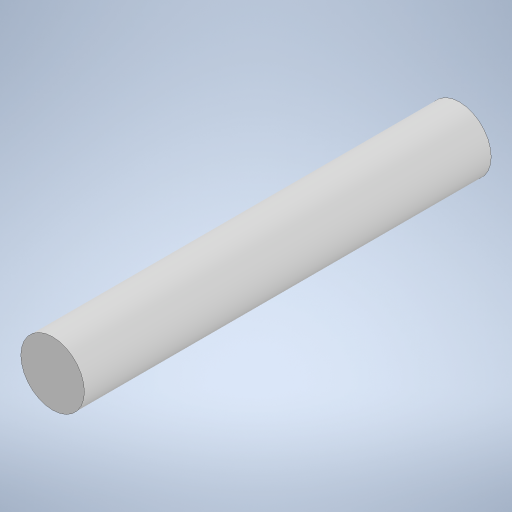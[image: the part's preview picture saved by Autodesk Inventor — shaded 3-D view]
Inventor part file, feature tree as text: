
AUTODESK INVENTOR PART (.ipt)
format: ipt  version: 2023 (Build 270158000, 158)  size: 217,088 bytes
history: native  units: in
note: dims shown in document units (in); Inventor stores cm internally (conversion verified against a paired STEP export)
features: extrude x1, sketch x1
ambient origin geometry x8: Origin, YZ Plane, XZ Plane, XY Plane, X Axis, Y Axis, Z Axis, Center Point
bodies: Solid1 (feature_tree)
feature tree (2):
  extrude  "Extrusion1"  Depth=0.2in TaperAngle=0.0deg
  sketch  "Sketch1"  dims[d0=0.0312in d1=0.2in d2=0.0in]
